# Revit family: FU_Chair_Sandler_Timber 2-1
name_source: partatom
category: Furniture
units: mm (PartAtom-declared; Revit-internal decimal feet)

## family parameters
Always vertical = Yes
Cut with Voids When Loaded = No
OmniClass Number = 23.40.20.00
OmniClass Title = General Furniture and Specialties
Room Calculation Point = No
Shared = No
Work Plane-Based = No

## types (2) — shared parameters
Frame = Wood - Beech - Walnut - V
Manufacturer = Sandler
URL = https://www.sandlerseating.com
zero-valued in all types: Default Elevation

## per-type parameters (varying)
| type | Depth | Description | Height | Seat | Uph_IsVisible | Width |
| Timber 1.2 | 520 mm  [stored 1.70604 ft] | Side chair with an upholstered seat and wooden back on a solid beech frame. | 795 mm  [stored 2.60827 ft] | <By Category> | Yes | 510 mm  [stored 1.67323 ft] |
| Timber 2.1 | 560 mm  [stored 1.83727 ft] | Armchair with wooden seat and back on a solid beech frame. | 860 mm | Wood -  Aniline - Gray | No | 635 mm |

note: column(s) folded — value = type name in every type: Model

note: [stored X ft] marks values corroborated as IEEE doubles in the binary element streams (Revit-internal decimal feet)

## geometry (parser evidence)
native form markers: Sweep x4
no freeform markers — native parametric forms only
